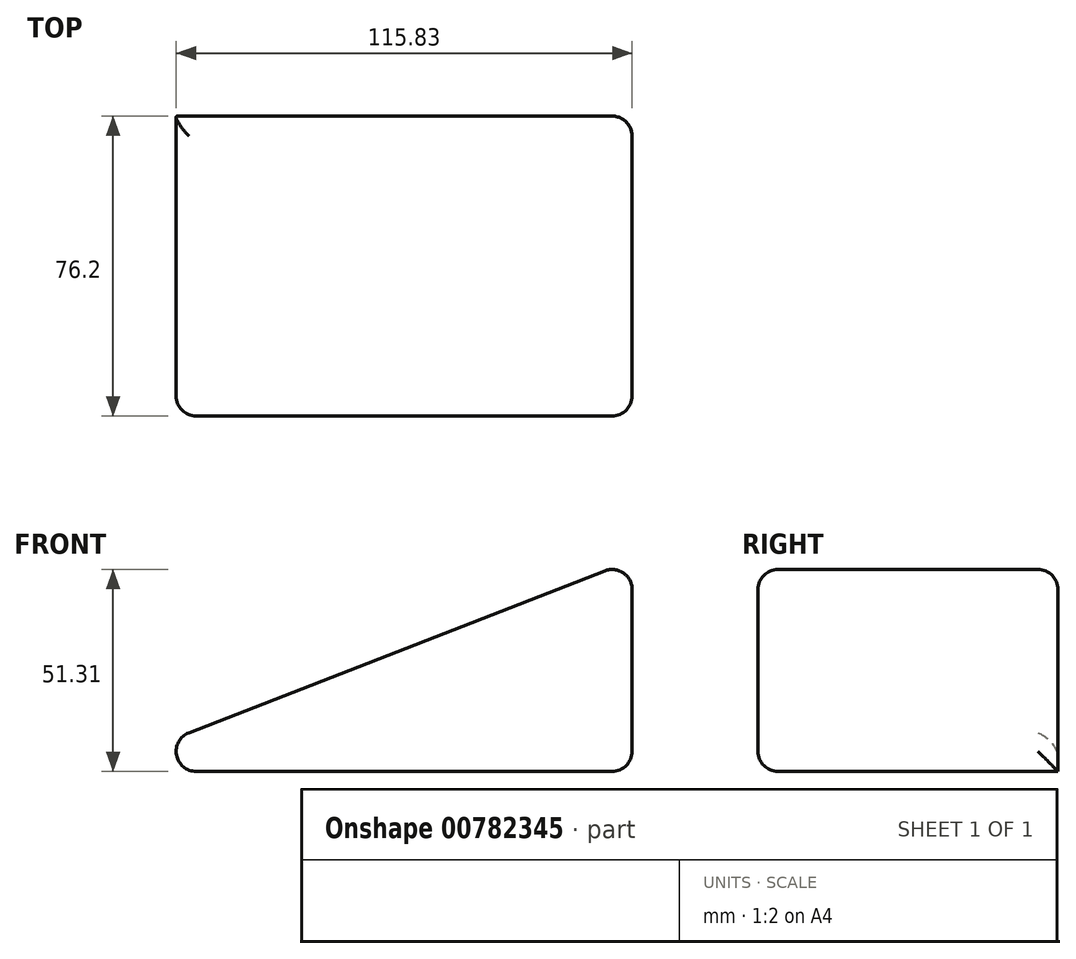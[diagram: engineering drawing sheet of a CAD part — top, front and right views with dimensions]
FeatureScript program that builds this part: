
annotation { "Feature Type Name" : "Feature", "Feature Type Description" : "" }
export const myFeature = defineFeature(function(context is Context, id is Id, definition is map)
    precondition{}
    {
        {
            var Q0;
            Q0=qCreatedBy(makeId("Front.planeOp"),FACE);
            var sketch = newSketch(context, id + "F0", { "sketchPlane" : qUnion([Q0])});
            skLineSegment(sketch, "E0.bottom", {"start": v(68.9, -26.83) * mm, "end": v(-68.9, -26.83) * mm});
            skLineSegment(sketch, "E0.left", {"start": v(68.9, -26.83) * mm, "end": v(68.9, 26.83) * mm});
            skPoint(sketch, "E0.middle", {"position": v(0, 0) * mm});
            skLineSegment(sketch, "E1", {"start": v(-68.9, -26.83) * mm, "end": v(68.9, 26.83) * mm});
            skPoint(sketch, "E0.right.end.orphan", {"position": v(-68.9, 26.83) * mm});
            skSolve(sketch);
        }
        {
            var Q0;
            Q0=makeQuery(id+"F0.imprint","IMPRINT",FACE,{"disambiguationData":[TD([[makeQuery(id+"F0.imprint","IMPRINT",EDGE,{"derivedFrom":sQuery(id+"F0.wireOp",EDGE,"E0.bottom")}),-1.0]])]});
            extrude(context, id + "F1", {"entities" : qUnion([Q0]), "depth" : 76.2 * mm, "offsetDistance" : 25.4 * mm});
        }
        {
            var Q0;
            Q0=makeQuery(id+"F1.opExtrude","CAP_EDGE",EDGE,{"disambiguationData":[OSD([sQuery(id+"F0.wireOp",EDGE,"E1")])],"isStart":false});
            var Q1;
            Q1=makeQuery(id+"F1.opExtrude","CAP_EDGE",EDGE,{"disambiguationData":[OSD([sQuery(id+"F0.wireOp",EDGE,"E1")])],"isStart":true});
            var Q2;
            Q2=makeQuery(id+"F1.opExtrude","CAP_EDGE",EDGE,{"disambiguationData":[OSD([sQuery(id+"F0.wireOp",EDGE,"E0.bottom")])],"isStart":false});
            var Q3;
            Q3=makeQuery(id+"F1.opExtrude","SWEPT_EDGE",EDGE,{"disambiguationData":[OSD([sQuery(id+"F0.wireOp",EDGE,"E0.bottom"),sQuery(id+"F0.wireOp",EDGE,"E1")])]});
            var Q4;
            Q4=makeQuery(id+"F1.opExtrude","CAP_EDGE",EDGE,{"disambiguationData":[OSD([sQuery(id+"F0.wireOp",EDGE,"E0.left")])],"isStart":false});
            var Q5;
            Q5=makeQuery(id+"F1.opExtrude","CAP_EDGE",EDGE,{"disambiguationData":[OSD([sQuery(id+"F0.wireOp",EDGE,"E0.left")])],"isStart":true});
            var Q6;
            Q6=makeQuery(id+"F1.opExtrude","SWEPT_EDGE",EDGE,{"disambiguationData":[OSD([sQuery(id+"F0.wireOp",EDGE,"E0.bottom"),sQuery(id+"F0.wireOp",EDGE,"E0.left")])]});
            var Q7;
            Q7=makeQuery(id+"F1.opExtrude","SWEPT_EDGE",EDGE,{"disambiguationData":[OSD([sQuery(id+"F0.wireOp",EDGE,"E0.left"),sQuery(id+"F0.wireOp",EDGE,"E1")])]});
            fillet(context, id + "F2", {"entities" : qUnion([Q0, Q1, Q2, Q3, Q4, Q5, Q6, Q7]), "radius" : 5.08 * mm, "tangentPropagation" : true, "allowEdgeOverflow" : false});
        }
    });
